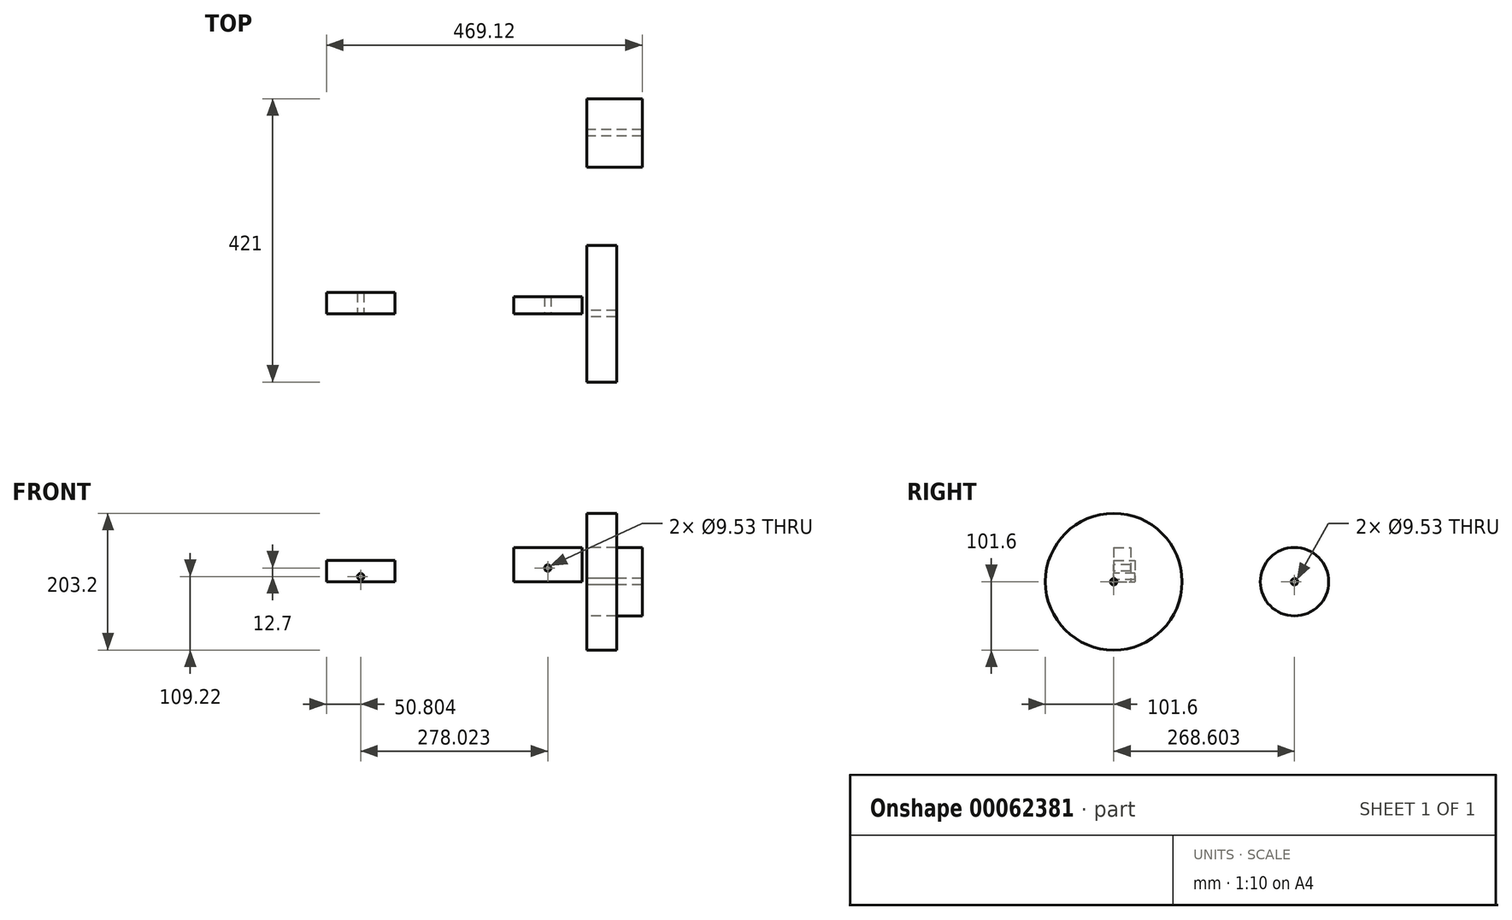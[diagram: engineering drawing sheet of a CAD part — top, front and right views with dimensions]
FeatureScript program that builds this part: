
annotation { "Feature Type Name" : "Feature", "Feature Type Description" : "" }
export const myFeature = defineFeature(function(context is Context, id is Id, definition is map)
    precondition{}
    {
        {
            var Q0;
            Q0=qCreatedBy(makeId("Right.planeOp"),FACE);
            var sketch = newSketch(context, id + "F0", { "sketchPlane" : qUnion([Q0])});
            skCircle(sketch, "E0", {"center": v(0, 0) * mm, "radius": 101.6 * mm});
            skCircle(sketch, "E1", {"center": v(0, 0) * mm, "radius": 4.76 * mm});
            skSolve(sketch);
        }
        {
            var Q0;
            Q0=makeQuery(id+"F0.imprint","IMPRINT",FACE,{"disambiguationData":[TD([[makeQuery(id+"F0.imprint","IMPRINT",EDGE,{"derivedFrom":sQuery(id+"F0.wireOp",EDGE,"E0")}),1.0]])]});
            extrude(context, id + "F1", {"entities" : qUnion([Q0]), "depth" : 44.45 * mm});
        }
        {
            var Q0;
            Q0=makeQuery(id+"F1.opExtrude","CAP_FACE",FACE,{"disambiguationData":[OSD([sQuery(id+"F0.wireOp",EDGE,"E0")])],"isStart":true});
            var sketch = newSketch(context, id + "F2", { "sketchPlane" : qUnion([Q0])});
            skCircle(sketch, "E2", {"center": v(-268.6, 0) * mm, "radius": 50.8 * mm});
            skCircle(sketch, "E3", {"center": v(-268.6, 0) * mm, "radius": 4.76 * mm});
            skSolve(sketch);
        }
        {
            var Q0;
            Q0=makeQuery(id+"F2.imprint","IMPRINT",FACE,{"disambiguationData":[TD([[makeQuery(id+"F2.imprint","IMPRINT",EDGE,{"derivedFrom":sQuery(id+"F2.wireOp",EDGE,"E2")}),1.0]])]});
            extrude(context, id + "F3", {"entities" : qUnion([Q0]), "oppositeDirection" : true, "depth" : 82.55 * mm});
        }
        {
            var Q0;
            Q0=qCreatedBy(makeId("Top.planeOp"),FACE);
            var sketch = newSketch(context, id + "F4", { "sketchPlane" : qUnion([Q0])});
            skLineSegment(sketch, "E4.bottom", {"start": v(-6.94, 0) * mm, "end": v(-108.54, 0) * mm});
            skLineSegment(sketch, "E4.top", {"start": v(-6.94, 25.4) * mm, "end": v(-108.54, 25.4) * mm});
            skLineSegment(sketch, "E4.left", {"start": v(-6.94, 0) * mm, "end": v(-6.94, 25.4) * mm});
            skLineSegment(sketch, "E4.right", {"start": v(-108.54, 0) * mm, "end": v(-108.54, 25.4) * mm});
            skSolve(sketch);
        }
        {
            var Q0;
            Q0=makeQuery(id+"F4.imprint","IMPRINT",FACE,{"disambiguationData":[TD([[makeQuery(id+"F4.imprint","IMPRINT",EDGE,{"derivedFrom":sQuery(id+"F4.wireOp",EDGE,"E4.bottom")}),-1.0]])]});
            extrude(context, id + "F5", {"entities" : qUnion([Q0]), "depth" : 50.8 * mm});
        }
        {
            var Q0;
            Q0=makeQuery(id+"F5.opExtrude","SWEPT_FACE",FACE,{"disambiguationData":[OSD([sQuery(id+"F4.wireOp",EDGE,"E4.bottom")])]});
            var sketch = newSketch(context, id + "F6", { "sketchPlane" : qUnion([Q0])});
            skCircle(sketch, "E5", {"center": v(-57.74, 20.32) * mm, "radius": 4.76 * mm});
            skPoint(sketch, "E5.centerSnap0", {"position": v(-57.74, 50.8) * mm});
            skSolve(sketch);
        }
        {
            var Q0;
            Q0=makeQuery(id+"F6.imprint","IMPRINT",FACE,{"disambiguationData":[TD([[makeQuery(id+"F6.imprint","IMPRINT",EDGE,{"derivedFrom":sQuery(id+"F6.wireOp",EDGE,"E5")}),1.0]])]});
            extrude(context, id + "F7", {"entities" : qUnion([Q0]), "operationType" : NewBodyOperationType.REMOVE, "endBound" : BoundingType.UP_TO_NEXT, "oppositeDirection" : true, "depth" : 25.4 * mm});
        }
        {
            var Q0;
            Q0=qCreatedBy(makeId("Top.planeOp"),FACE);
            var sketch = newSketch(context, id + "F8", { "sketchPlane" : qUnion([Q0])});
            skLineSegment(sketch, "E6.bottom", {"start": v(-284.97, 0) * mm, "end": v(-386.57, 0) * mm});
            skLineSegment(sketch, "E6.top", {"start": v(-284.97, 31.75) * mm, "end": v(-386.57, 31.75) * mm});
            skLineSegment(sketch, "E6.left", {"start": v(-284.97, 0) * mm, "end": v(-284.97, 31.75) * mm});
            skLineSegment(sketch, "E6.right", {"start": v(-386.57, 0) * mm, "end": v(-386.57, 31.75) * mm});
            skSolve(sketch);
        }
        {
            var Q0;
            Q0=makeQuery(id+"F8.imprint","IMPRINT",FACE,{"disambiguationData":[TD([[makeQuery(id+"F8.imprint","IMPRINT",EDGE,{"derivedFrom":sQuery(id+"F8.wireOp",EDGE,"E6.bottom")}),-1.0]])]});
            extrude(context, id + "F9", {"entities" : qUnion([Q0]), "depth" : 31.75 * mm});
        }
        {
            var Q0;
            Q0=makeQuery(id+"F9.opExtrude","SWEPT_FACE",FACE,{"disambiguationData":[OSD([sQuery(id+"F8.wireOp",EDGE,"E6.bottom")])]});
            var sketch = newSketch(context, id + "F10", { "sketchPlane" : qUnion([Q0])});
            skCircle(sketch, "E7", {"center": v(-335.77, 7.62) * mm, "radius": 4.76 * mm});
            skPoint(sketch, "E7.centerSnap0", {"position": v(-335.77, 0) * mm});
            skSolve(sketch);
        }
        {
            var Q0;
            Q0=makeQuery(id+"F10.imprint","IMPRINT",FACE,{"disambiguationData":[TD([[makeQuery(id+"F10.imprint","IMPRINT",EDGE,{"derivedFrom":sQuery(id+"F10.wireOp",EDGE,"E7")}),1.0]])]});
            extrude(context, id + "F11", {"entities" : qUnion([Q0]), "operationType" : NewBodyOperationType.REMOVE, "endBound" : BoundingType.UP_TO_NEXT, "oppositeDirection" : true, "depth" : 25.4 * mm});
        }
    });
